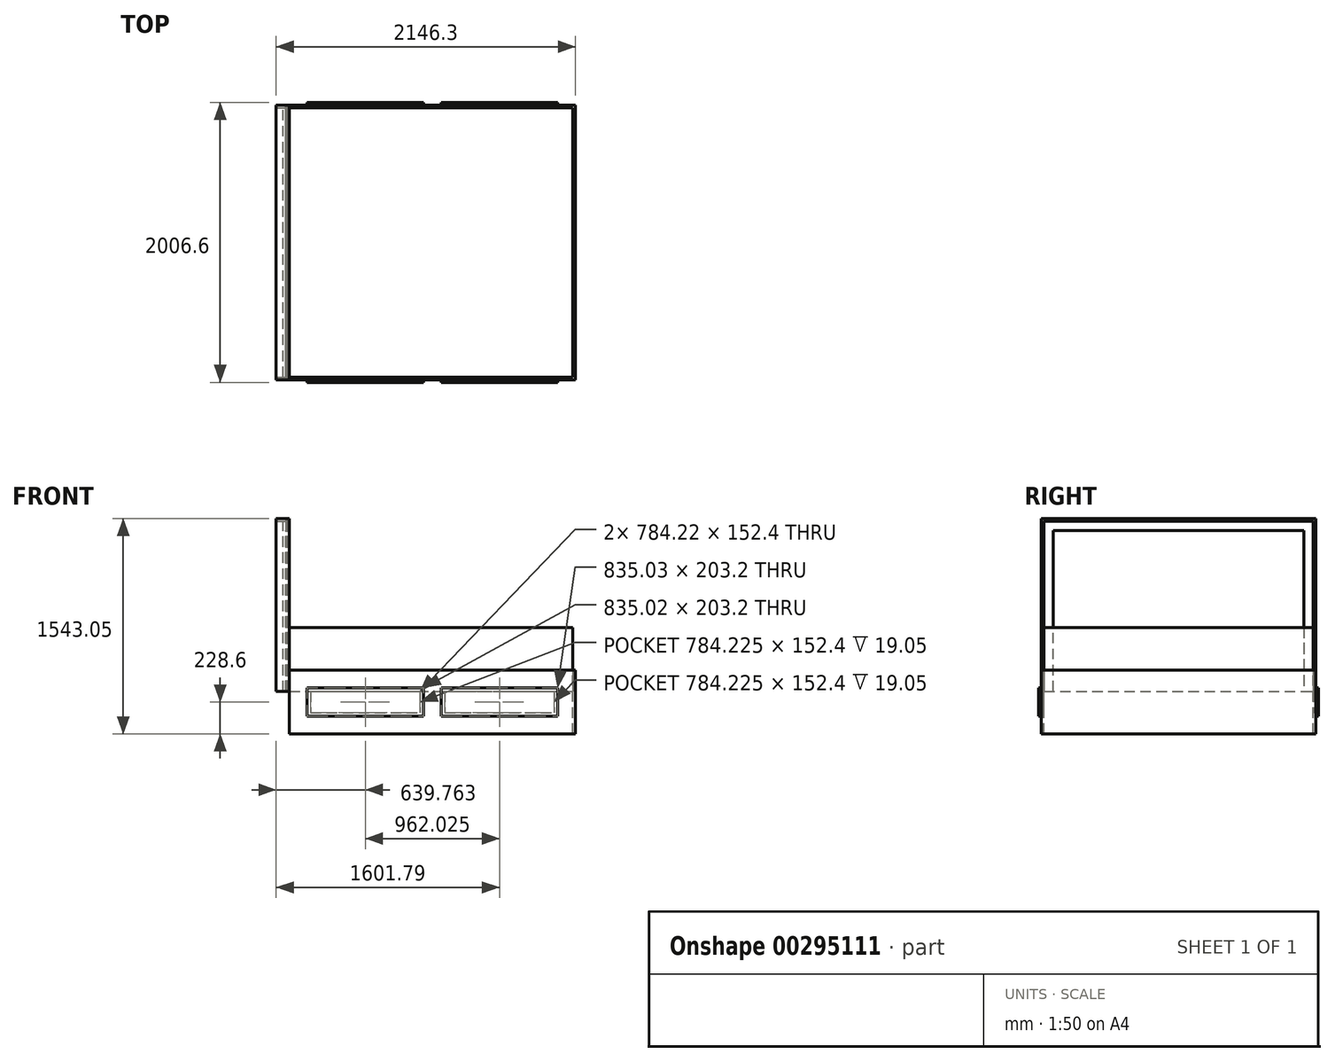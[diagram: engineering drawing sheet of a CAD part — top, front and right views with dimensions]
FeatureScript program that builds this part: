
annotation { "Feature Type Name" : "Feature", "Feature Type Description" : "" }
export const myFeature = defineFeature(function(context is Context, id is Id, definition is map)
    precondition{}
    {
        {
            var Q0;
            Q0=qCreatedBy(makeId("Right.planeOp"),FACE);
            var sketch = newSketch(context, id + "F0", { "sketchPlane" : qUnion([Q0])});
            skLineSegment(sketch, "E0.bottom", {"start": v(-965.2, 0) * mm, "end": v(965.2, 0) * mm});
            skLineSegment(sketch, "E0.top", {"start": v(-965.2, 1219.2) * mm, "end": v(965.2, 1219.2) * mm});
            skLineSegment(sketch, "E0.left", {"start": v(-965.2, 0) * mm, "end": v(-965.2, 1219.2) * mm});
            skLineSegment(sketch, "E0.right", {"start": v(965.2, 0) * mm, "end": v(965.2, 1219.2) * mm});
            skSolve(sketch);
        }
        {
            var Q0;
            Q0 = qSketchRegion(id + "F0", true);
            extrude(context, id + "F1", {"entities" : qUnion([Q0]), "oppositeDirection" : true, "depth" : 19.05 * mm});
        }
        {
            var Q0;
            Q0=makeQuery(id+"F1.opExtrude","CAP_FACE",FACE,{"disambiguationData":[OSD([sQuery(id+"F0.wireOp",EDGE,"E0.bottom"),sQuery(id+"F0.wireOp",EDGE,"E0.top"),sQuery(id+"F0.wireOp",EDGE,"E0.left"),sQuery(id+"F0.wireOp",EDGE,"E0.right")])],"isStart":true});
            cPlane(context, id + "F2", {"entities" : qUnion([Q0]), "cplaneType" : CPlaneType.OFFSET, "offset" : 12.7 * mm, "width" : 152.4 * mm, "height" : 152.4 * mm});
        }
        {
            var Q0;
            Q0=qCreatedBy(id+"F2.planeOp",FACE);
            var sketch = newSketch(context, id + "F3", { "sketchPlane" : qUnion([Q0])});
            skLineSegment(sketch, "E1.bottom", {"start": v(-965.2, 0) * mm, "end": v(-984.25, 0) * mm});
            skLineSegment(sketch, "E1.left", {"start": v(-965.2, 0) * mm, "end": v(-965.2, 1219.2) * mm});
            skLineSegment(sketch, "E1.right", {"start": v(-984.25, 0) * mm, "end": v(-984.25, 1238.25) * mm});
            skLineSegment(sketch, "E2", {"start": v(-984.25, 1238.25) * mm, "end": v(-965.2, 1219.2) * mm});
            skLineSegment(sketch, "E3", {"start": v(-984.25, 1238.25) * mm, "end": v(984.25, 1238.25) * mm});
            skLineSegment(sketch, "E4", {"start": v(984.25, 1238.25) * mm, "end": v(965.2, 1219.2) * mm});
            skLineSegment(sketch, "E5", {"start": v(965.2, 1219.2) * mm, "end": v(-965.2, 1219.2) * mm});
            skLineSegment(sketch, "E6", {"start": v(984.25, 1238.25) * mm, "end": v(984.25, 0) * mm});
            skLineSegment(sketch, "E7", {"start": v(984.25, 0) * mm, "end": v(965.2, 0) * mm});
            skLineSegment(sketch, "E8", {"start": v(965.2, 0) * mm, "end": v(965.2, 1219.2) * mm});
            skSolve(sketch);
        }
        {
            var Q0;
            Q0 = qSketchRegion(id + "F3", true);
            extrude(context, id + "F4", {"entities" : qUnion([Q0]), "oppositeDirection" : true, "depth" : 82.55 * mm, "hasSecondDirection" : true, "secondDirectionOppositeDirection" : false, "secondDirectionDepth" : 12.7 * mm});
        }
        {
            var Q0;
            Q0=makeQuery(id+"F1.opExtrude","CAP_FACE",FACE,{"disambiguationData":[OSD([sQuery(id+"F0.wireOp",EDGE,"E0.bottom"),sQuery(id+"F0.wireOp",EDGE,"E0.top"),sQuery(id+"F0.wireOp",EDGE,"E0.left"),sQuery(id+"F0.wireOp",EDGE,"E0.right")])],"isStart":true});
            var sketch = newSketch(context, id + "F5", { "sketchPlane" : qUnion([Q0])});
            skLineSegment(sketch, "E9.bottom", {"start": v(-974.72, 0) * mm, "end": v(974.72, 0) * mm});
            skLineSegment(sketch, "E9.top", {"start": v(-974.73, 1228.72) * mm, "end": v(974.72, 1228.73) * mm});
            skLineSegment(sketch, "E9.left", {"start": v(-974.73, 0) * mm, "end": v(-974.73, 1228.72) * mm});
            skLineSegment(sketch, "E9.right", {"start": v(974.73, 0) * mm, "end": v(974.73, 1228.73) * mm});
            skSolve(sketch);
        }
        {
            var Q0;
            Q0 = qSketchRegion(id + "F5", true);
            extrude(context, id + "F6", {"entities" : qUnion([Q0]), "operationType" : NewBodyOperationType.REMOVE, "depth" : 12.7 * mm});
        }
        {
            var Q0;
            Q0=makeQuery(id+"F1.opExtrude","CAP_FACE",FACE,{"disambiguationData":[OSD([sQuery(id+"F0.wireOp",EDGE,"E0.bottom"),sQuery(id+"F0.wireOp",EDGE,"E0.top"),sQuery(id+"F0.wireOp",EDGE,"E0.left"),sQuery(id+"F0.wireOp",EDGE,"E0.right")])],"isStart":true});
            var sketch = newSketch(context, id + "F7", { "sketchPlane" : qUnion([Q0])});
            skLineSegment(sketch, "E10", {"start": v(-974.73, 0) * mm, "end": v(-898.53, 0) * mm});
            skLineSegment(sketch, "E11", {"start": v(-898.53, 0) * mm, "end": v(-898.53, 1152.52) * mm});
            skLineSegment(sketch, "E12", {"start": v(-898.53, 1152.52) * mm, "end": v(898.52, 1152.52) * mm});
            skLineSegment(sketch, "E13", {"start": v(898.52, 1152.52) * mm, "end": v(898.52, 0) * mm});
            skLineSegment(sketch, "E14", {"start": v(898.52, 0) * mm, "end": v(974.72, 0) * mm});
            skLineSegment(sketch, "E15", {"start": v(974.72, 0) * mm, "end": v(974.72, 1228.73) * mm});
            skLineSegment(sketch, "E16", {"start": v(974.72, 1228.73) * mm, "end": v(-974.73, 1228.72) * mm});
            skLineSegment(sketch, "E17", {"start": v(-974.73, 1228.72) * mm, "end": v(-974.73, 0) * mm});
            skSolve(sketch);
        }
        {
            var Q0;
            Q0 = qSketchRegion(id + "F7", true);
            extrude(context, id + "F8", {"entities" : qUnion([Q0]), "depth" : 12.7 * mm});
        }
        {
            var Q0;
            Q0=qCreatedBy(makeId("Top.planeOp"),FACE);
            var sketch = newSketch(context, id + "F9", { "sketchPlane" : qUnion([Q0])});
            skLineSegment(sketch, "E18.bottom", {"start": v(25.4, -965.2) * mm, "end": v(2057.4, -965.2) * mm});
            skLineSegment(sketch, "E18.top", {"start": v(25.4, 965.2) * mm, "end": v(2057.4, 965.2) * mm});
            skLineSegment(sketch, "E18.left", {"start": v(25.4, -965.2) * mm, "end": v(25.4, 965.2) * mm});
            skLineSegment(sketch, "E18.right", {"start": v(2057.4, -965.2) * mm, "end": v(2057.4, 965.2) * mm});
            skSolve(sketch);
        }
        {
            var Q0;
            Q0 = qSketchRegion(id + "F9", true);
            extrude(context, id + "F10", {"entities" : qUnion([Q0]), "depth" : 457.2 * mm});
        }
        {
            var Q0;
            Q0=makeQuery(id+"F10.opExtrude","CAP_FACE",FACE,{"disambiguationData":[OSD([sQuery(id+"F9.wireOp",EDGE,"E18.bottom"),sQuery(id+"F9.wireOp",EDGE,"E18.top"),sQuery(id+"F9.wireOp",EDGE,"E18.left"),sQuery(id+"F9.wireOp",EDGE,"E18.right")])],"isStart":false});
            cPlane(context, id + "F11", {"entities" : qUnion([Q0]), "cplaneType" : CPlaneType.OFFSET, "offset" : 304.8 * mm, "oppositeDirection" : true, "width" : 152.4 * mm, "height" : 152.4 * mm});
        }
        {
            var Q0;
            Q0=qCreatedBy(id+"F11.planeOp",FACE);
            var sketch = newSketch(context, id + "F12", { "sketchPlane" : qUnion([Q0])});
            skLineSegment(sketch, "E19", {"start": v(25.4, -984.25) * mm, "end": v(2076.45, -984.25) * mm});
            skLineSegment(sketch, "E20", {"start": v(2076.45, -984.25) * mm, "end": v(2076.45, 984.25) * mm});
            skLineSegment(sketch, "E21", {"start": v(2076.45, 984.25) * mm, "end": v(25.4, 984.25) * mm});
            skLineSegment(sketch, "E22", {"start": v(25.4, 984.25) * mm, "end": v(25.4, 965.2) * mm});
            skLineSegment(sketch, "E23", {"start": v(25.4, 965.2) * mm, "end": v(2057.4, 965.2) * mm});
            skLineSegment(sketch, "E24", {"start": v(2057.4, 965.2) * mm, "end": v(2057.4, -965.2) * mm});
            skLineSegment(sketch, "E25", {"start": v(2057.4, -965.2) * mm, "end": v(25.4, -965.2) * mm});
            skLineSegment(sketch, "E26", {"start": v(25.4, -965.2) * mm, "end": v(25.4, -984.25) * mm});
            skSolve(sketch);
        }
        {
            var Q0;
            Q0 = qSketchRegion(id + "F12", true);
            extrude(context, id + "F13", {"entities" : qUnion([Q0]), "oppositeDirection" : true, "depth" : 457.2 * mm});
        }
        {
            var Q0;
            Q0=makeQuery(id+"F13.opExtrude","SWEPT_FACE",FACE,{"disambiguationData":[OSD([sQuery(id+"F12.wireOp",EDGE,"E19")])]});
            var sketch = newSketch(context, id + "F14", { "sketchPlane" : qUnion([Q0])});
            skLineSegment(sketch, "E27.bottom", {"start": v(177.8, 0) * mm, "end": v(962.03, 0) * mm});
            skLineSegment(sketch, "E27.top", {"start": v(177.8, -152.4) * mm, "end": v(962.03, -152.4) * mm});
            skLineSegment(sketch, "E27.left", {"start": v(177.8, 0) * mm, "end": v(177.8, -152.4) * mm});
            skLineSegment(sketch, "E27.right", {"start": v(1924.05, 0) * mm, "end": v(1924.05, -152.4) * mm});
            skLineSegment(sketch, "E28", {"start": v(962.03, 0) * mm, "end": v(962.03, -152.4) * mm});
            skLineSegment(sketch, "E29", {"start": v(1139.82, 0) * mm, "end": v(1139.82, -152.4) * mm});
            skLineSegment(sketch, "E30.trimOffspring", {"start": v(1139.82, 0) * mm, "end": v(1924.05, 0) * mm});
            skLineSegment(sketch, "E31.trimOffspring", {"start": v(1139.82, -152.4) * mm, "end": v(1924.05, -152.4) * mm});
            skSolve(sketch);
        }
        {
            var Q0;
            Q0 = qSketchRegion(id + "F14", true);
            extrude(context, id + "F15", {"entities" : qUnion([Q0]), "operationType" : NewBodyOperationType.REMOVE, "oppositeDirection" : true, "depth" : 2540 * mm});
        }
        {
            var Q0;
            Q0=makeQuery(id+"F13.opExtrude","SWEPT_FACE",FACE,{"disambiguationData":[OSD([sQuery(id+"F12.wireOp",EDGE,"E19")])]});
            var sketch = newSketch(context, id + "F16", { "sketchPlane" : qUnion([Q0])});
            skLineSegment(sketch, "E32.bottom", {"start": v(152.4, 25.4) * mm, "end": v(987.43, 25.4) * mm});
            skLineSegment(sketch, "E32.top", {"start": v(152.4, -177.8) * mm, "end": v(987.43, -177.8) * mm});
            skLineSegment(sketch, "E32.left", {"start": v(152.4, 25.4) * mm, "end": v(152.4, -177.8) * mm});
            skLineSegment(sketch, "E32.right", {"start": v(987.43, 25.4) * mm, "end": v(987.43, -177.8) * mm});
            skLineSegment(sketch, "E33.bottom", {"start": v(1114.42, 25.4) * mm, "end": v(1949.45, 25.4) * mm});
            skLineSegment(sketch, "E33.top", {"start": v(1114.42, -177.8) * mm, "end": v(1949.45, -177.8) * mm});
            skLineSegment(sketch, "E33.left", {"start": v(1114.42, 25.4) * mm, "end": v(1114.42, -177.8) * mm});
            skLineSegment(sketch, "E33.right", {"start": v(1949.45, 25.4) * mm, "end": v(1949.45, -177.8) * mm});
            skSolve(sketch);
        }
        {
            var Q0;
            Q0 = qSketchRegion(id + "F16", true);
            extrude(context, id + "F17", {"entities" : qUnion([Q0]), "depth" : 19.05 * mm});
        }
        {
            var Q0;
            Q0=makeQuery(id+"F17.opExtrude","SWEPT_BODY",BODY,{"disambiguationData":[OSD([sQuery(id+"F16.wireOp",EDGE,"E32.bottom"),sQuery(id+"F16.wireOp",EDGE,"E32.top"),sQuery(id+"F16.wireOp",EDGE,"E32.left"),sQuery(id+"F16.wireOp",EDGE,"E32.right")])]});
            var Q1;
            Q1=makeQuery(id+"F17.opExtrude","SWEPT_BODY",BODY,{"disambiguationData":[OSD([sQuery(id+"F16.wireOp",EDGE,"E33.bottom"),sQuery(id+"F16.wireOp",EDGE,"E33.top"),sQuery(id+"F16.wireOp",EDGE,"E33.left"),sQuery(id+"F16.wireOp",EDGE,"E33.right")])]});
            var Q2;
            Q2=qCreatedBy(makeId("Front.planeOp"),FACE);
            mirror(context, id + "F18", {"operationType" : NewBodyOperationType.ADD, "entities" : qUnion([Q0, Q1]), "mirrorPlane" : qUnion([Q2])});
        }
    });
